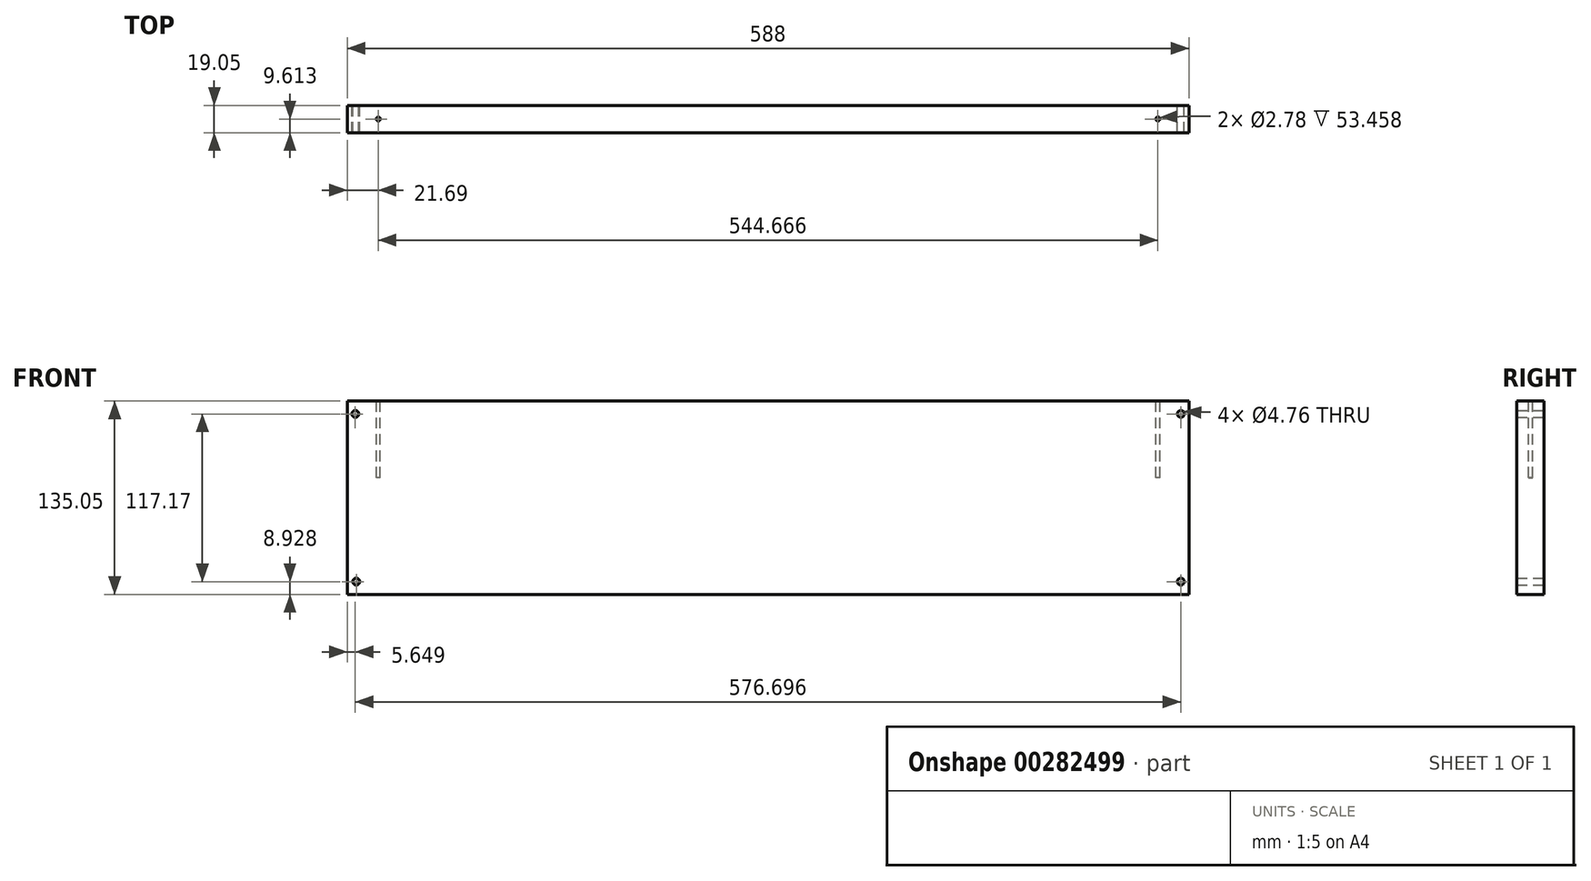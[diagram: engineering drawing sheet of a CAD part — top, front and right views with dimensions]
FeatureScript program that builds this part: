
annotation { "Feature Type Name" : "Feature", "Feature Type Description" : "" }
export const myFeature = defineFeature(function(context is Context, id is Id, definition is map)
    precondition{}
    {
        {
            var Q0;
            Q0=qCreatedBy(makeId("Front.planeOp"),FACE);
            var sketch = newSketch(context, id + "F0", { "sketchPlane" : qUnion([Q0])});
            skLineSegment(sketch, "E0.bottom", {"start": v(-297.52, -16.54) * mm, "end": v(290.48, -16.54) * mm});
            skLineSegment(sketch, "E0.top", {"start": v(-297.52, -151.6) * mm, "end": v(290.48, -151.6) * mm});
            skLineSegment(sketch, "E0.left", {"start": v(-297.52, -16.54) * mm, "end": v(-297.52, -151.6) * mm});
            skLineSegment(sketch, "E0.right", {"start": v(290.48, -16.54) * mm, "end": v(290.48, -151.6) * mm});
            skCircle(sketch, "E1", {"center": v(-291.87, -25.5) * mm, "radius": 2.38 * mm});
            skCircle(sketch, "E2", {"center": v(-291.19, -142.64) * mm, "radius": 2.38 * mm});
            skCircle(sketch, "E3", {"center": v(284.83, -25.5) * mm, "radius": 2.38 * mm});
            skCircle(sketch, "E4", {"center": v(284.83, -142.66) * mm, "radius": 2.38 * mm});
            skSolve(sketch);
        }
        {
            var Q0;
            Q0=makeQuery(id+"F0.imprint","IMPRINT",FACE,{"disambiguationData":[TD([[makeQuery(id+"F0.imprint","IMPRINT",EDGE,{"derivedFrom":sQuery(id+"F0.wireOp",EDGE,"E0.bottom")}),-1.0]])]});
            extrude(context, id + "F1", {"entities" : qUnion([Q0]), "depth" : 19.05 * mm});
        }
        {
            var Q0;
            Q0=qCreatedBy(makeId("Top.planeOp"),FACE);
            var sketch = newSketch(context, id + "F2", { "sketchPlane" : qUnion([Q0])});
            skCircle(sketch, "E5", {"center": v(-275.83, -9.44) * mm, "radius": 1.39 * mm});
            skLineSegment(sketch, "E6", {"start": v(-3.5, 0) * mm, "end": v(-3.5, -22.22) * mm, "construction": true});
            skCircle(sketch, "E7.MirrorC", {"center": v(268.84, -9.44) * mm, "radius": 1.39 * mm});
            skLineSegment(sketch, "E8.bottom", {"start": v(-297.3, 0) * mm, "end": v(-278.2, 0) * mm, "construction": true});
            skLineSegment(sketch, "E8.top", {"start": v(-297.3, -18.7) * mm, "end": v(-278.2, -18.7) * mm, "construction": true});
            skLineSegment(sketch, "E8.left", {"start": v(-297.3, 0) * mm, "end": v(-297.3, -18.7) * mm, "construction": true});
            skLineSegment(sketch, "E8.right", {"start": v(-278.2, 0) * mm, "end": v(-278.2, -18.7) * mm, "construction": true});
            skSolve(sketch);
        }
        {
            var Q0;
            Q0=qSketchRegion(id+"F2",true);
            extrude(context, id + "F3", {"entities" : qUnion([Q0]), "operationType" : NewBodyOperationType.REMOVE, "oppositeDirection" : true, "depth" : 70 * mm});
        }
        {
            var Q0;
            Q0=qSketchRegion(id+"F0",true);
            extrude(context, id + "F4", {"entities" : qUnion([Q0]), "operationType" : NewBodyOperationType.REMOVE, "oppositeDirection" : true, "depth" : 19.05 * mm});
        }
        {
            var Q0;
            Q0=qSketchRegion(id+"F2",true);
            extrude(context, id + "F5", {"entities" : qUnion([Q0]), "operationType" : NewBodyOperationType.REMOVE, "oppositeDirection" : true, "depth" : 70 * mm});
        }
    });
